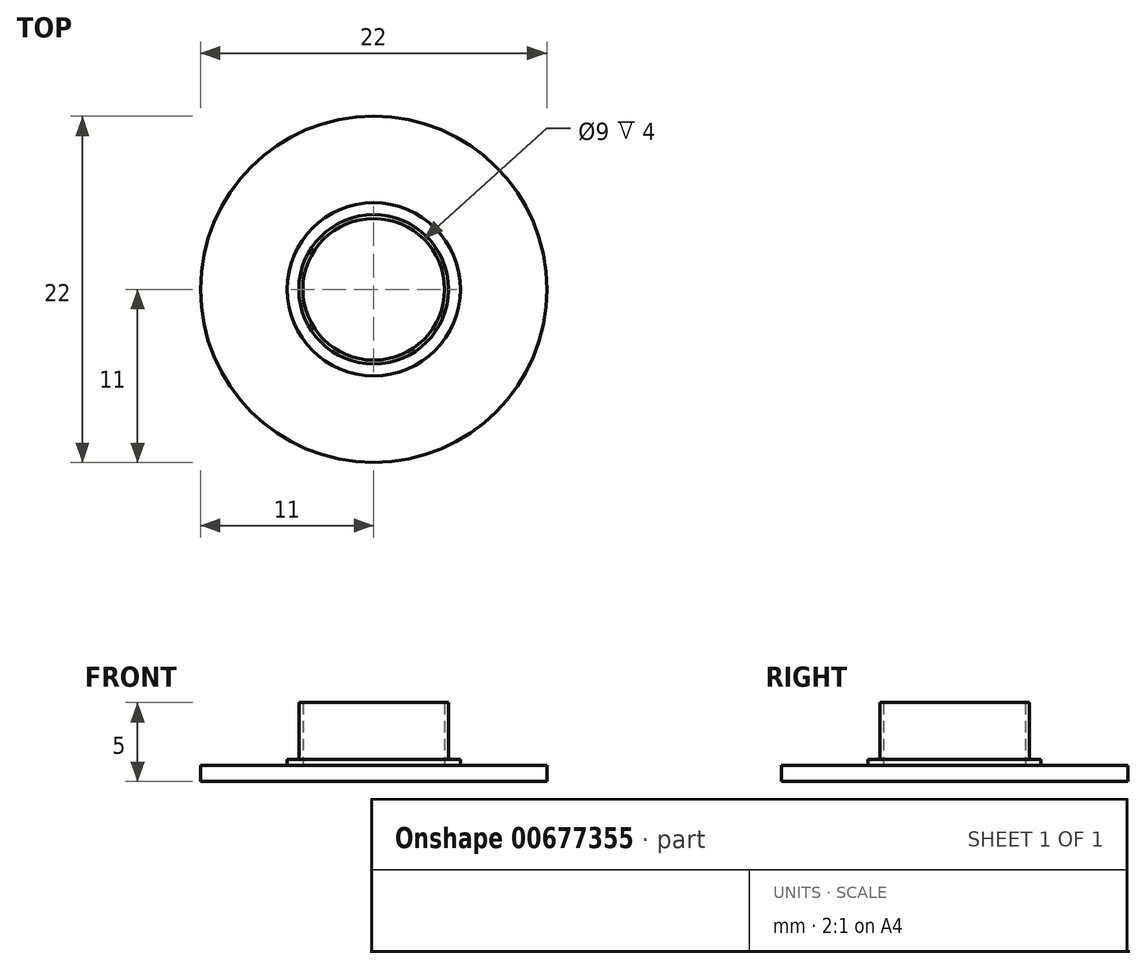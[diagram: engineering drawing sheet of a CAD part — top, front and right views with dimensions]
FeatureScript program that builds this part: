
annotation { "Feature Type Name" : "Feature", "Feature Type Description" : "" }
export const myFeature = defineFeature(function(context is Context, id is Id, definition is map)
    precondition{}
    {
        {
            var Q0;
            Q0=qCreatedBy(makeId("Top.planeOp"),FACE);
            var sketch = newSketch(context, id + "F0", { "sketchPlane" : qUnion([Q0])});
            skCircle(sketch, "E0", {"center": v(0, 0) * mm, "radius": 11 * mm});
            skCircle(sketch, "E1", {"center": v(0, 0) * mm, "radius": 5.5 * mm});
            skCircle(sketch, "E2", {"center": v(0, 0) * mm, "radius": 4.5 * mm});
            skCircle(sketch, "E3", {"center": v(0, 0) * mm, "radius": 4.75 * mm});
            skSolve(sketch);
        }
        {
            var Q0;
            Q0 = qSketchRegion(id + "F0", true);
            extrude(context, id + "F1", {"entities" : qUnion([Q0]), "depth" : 1 * mm, "offsetDistance" : 25 * mm});
        }
        {
            var Q0;
            Q0=makeQuery(id+"F0.imprint","IMPRINT",FACE,{"disambiguationData":[TD([[makeQuery(id+"F0.imprint","IMPRINT",EDGE,{"derivedFrom":sQuery(id+"F0.wireOp",EDGE,"E1")}),1.0]])]});
            var Q1;
            Q1=makeQuery(id+"F0.imprint","IMPRINT",FACE,{"disambiguationData":[TD([[makeQuery(id+"F0.imprint","IMPRINT",EDGE,{"derivedFrom":sQuery(id+"F0.wireOp",EDGE,"E2")}),-1.0]])]});
            extrude(context, id + "F2", {"entities" : qUnion([Q0, Q1]), "operationType" : NewBodyOperationType.ADD, "depth" : 1.4 * mm, "offsetDistance" : 25 * mm});
        }
        {
            var Q0;
            Q0=makeQuery(id+"F0.imprint","IMPRINT",FACE,{"disambiguationData":[TD([[makeQuery(id+"F0.imprint","IMPRINT",EDGE,{"derivedFrom":sQuery(id+"F0.wireOp",EDGE,"E2")}),-1.0]])]});
            extrude(context, id + "F3", {"entities" : qUnion([Q0]), "operationType" : NewBodyOperationType.ADD, "depth" : 5 * mm, "offsetDistance" : 25 * mm});
        }
        {
            var Q0;
            Q0=makeQuery(id+"F0.imprint","IMPRINT",FACE,{"disambiguationData":[TD([[makeQuery(id+"F0.imprint","IMPRINT",EDGE,{"derivedFrom":sQuery(id+"F0.wireOp",EDGE,"E2")}),1.0]])]});
            extrude(context, id + "F4", {"entities" : qUnion([Q0]), "operationType" : NewBodyOperationType.ADD, "depth" : 1 * mm, "offsetDistance" : 25 * mm});
        }
    });
